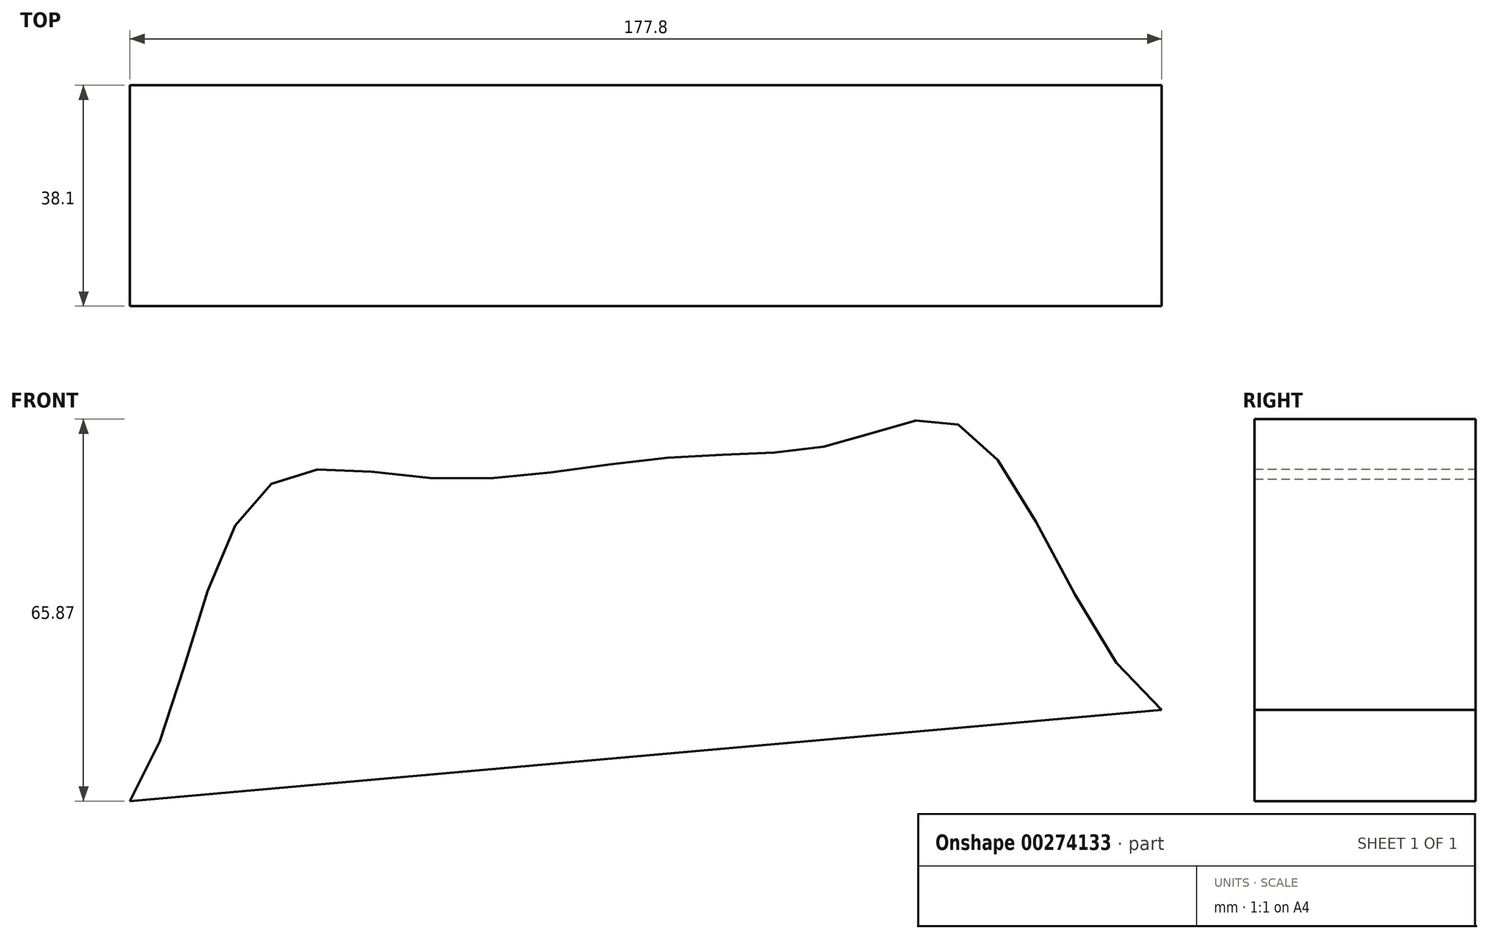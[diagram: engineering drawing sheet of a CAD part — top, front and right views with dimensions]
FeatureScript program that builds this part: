
annotation { "Feature Type Name" : "Feature", "Feature Type Description" : "" }
export const myFeature = defineFeature(function(context is Context, id is Id, definition is map)
    precondition{}
    {
        {
            var Q0;
            Q0=qCreatedBy(makeId("Front.planeOp"),FACE);
            var sketch = newSketch(context, id + "F0", { "sketchPlane" : qUnion([Q0])});
            skFitSpline(sketch, "E0", {"points": [v(54.96, -14.62) * mm, v(21.86, 33.45) * mm, v(0, 31.5) * mm, v(-30.13, 28.84) * mm, v(-70.26, 25.28) * mm, v(-100.7, 22.59) * mm, v(-122.84, -30.37) * mm], "startDerivative": vector(-191.18, 124.2) * mm, "endDerivative": vector(-134.55, -189.38) * mm});
            skLineSegment(sketch, "E1", {"start": v(-122.84, -30.37) * mm, "end": v(54.96, -14.62) * mm});
            skSolve(sketch);
        }
        {
            var Q0;
            Q0=makeQuery(id+"F0.imprint","IMPRINT",FACE,{"disambiguationData":[TD([[makeQuery(id+"F0.imprint","IMPRINT",EDGE,{"derivedFrom":sQuery(id+"F0.wireOp",EDGE,"E0")}),1.0]])]});
            extrude(context, id + "F1", {"entities" : qUnion([Q0]), "depth" : 38.1 * mm});
        }
    });
